# Revit family: NLRS_57_AIR_UN_steel penthouse louvre bdxn exhaust LT_sacs
name_source: partatom
category: Air Terminals
revit_build: Autodesk Revit 2018 (Build: 20190510_1515(x64)
units: mm (PartAtom-declared; Revit-internal decimal feet)

## family parameters
Always vertical = Yes
Cut with Voids When Loaded = No
Part Type = Normal
Room Calculation Point = No
Round Connector Dimension = Use Diameter
Shared = Yes
Work Plane-Based = No

## types (2) — shared parameters
Assembly Code = 57.0
Description = Solid Air Penthouse louvre BDXN (exhaust)
FireRating = 0
IfcDescription = Solid Air Penthouse louvre BDXN (exhaust)
IfcExportAs = IfcAirTerminal
IfcExportType = LOUVRE
IsExternal = Yes
LoadBearing = No
LookupTable = BDX
Manufacturer = Solid Air Climate Solutions
NLRS_C_content_datum_uitgifte = 29-04-2021
NLRS_C_content_provider = Solid Air Climate Solutions
NLRS_C_content_versie = 3.18.01
NLRS_C_niveau ontwikkeling = LOD 400
URL = https://solid-air.nl

## per-type parameters (varying)
| type | SACS_Base_Index | SACS_Factor_LpF1 | SACS_Factor_LpF2 | SACS_Factor_PsF1 | SACS_Factor_PsF2 | SACS_Option_1 |
| BDXNGO | 1 | 2.324406 | 26.035116 | 1.20867 | 2.001453 | Galvanised wire mesh |
| BDXNSO | 2 | 8.596469 | 26.019588 | 2.15725 | 1.999526 | RVS wire mesh |

note: column(s) folded — value = type name in every type: Model

## geometry (parser evidence)
native form markers: Sweep x20
no freeform markers — native parametric forms only
